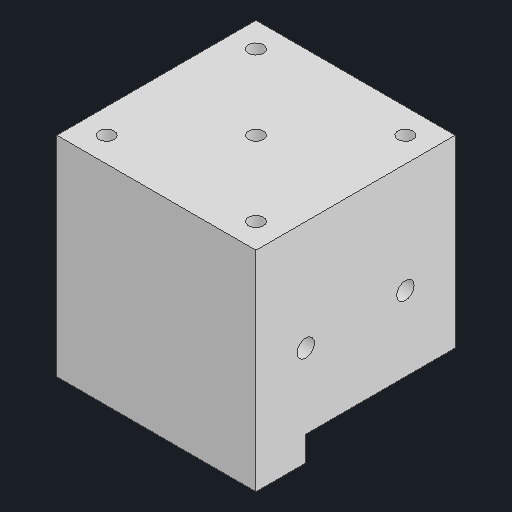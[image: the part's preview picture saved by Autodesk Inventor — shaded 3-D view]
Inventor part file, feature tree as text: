
AUTODESK INVENTOR PART (.ipt)
format: ipt  version: 2025.1 (Build 291241000, 241)  size: 130,048 bytes
history: native  units: mm
features: other x3, sketch x1
ambient origin geometry x8: Origin, YZ Plane, XZ Plane, XY Plane, X Axis, Y Axis, Z Axis, Center Point
bodies: Solid1 (feature_tree)
feature tree (4):
  other  "X Axis End.ipt"
  other  "Solid1::X Axis End.ipt"
  other  "TaggingFeature1"
  sketch  "Sketch1"  dims[d0=10.0mm]
